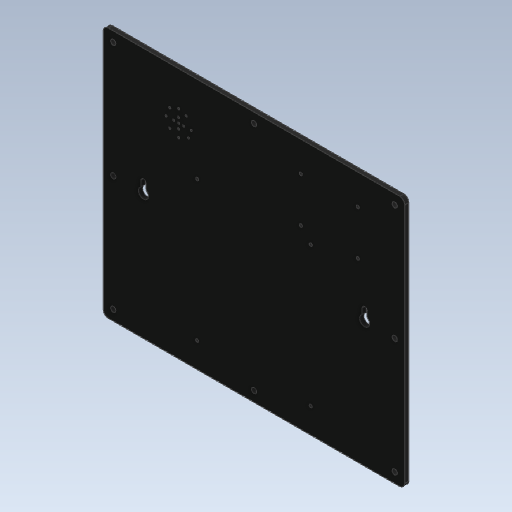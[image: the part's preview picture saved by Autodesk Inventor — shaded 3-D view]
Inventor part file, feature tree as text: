
AUTODESK INVENTOR PART (.ipt)
format: ipt  version: 2020 (Build 240168000, 168)  size: 320,000 bytes
history: native  units: mm
features: extrude x6, sketch x6, fillet x1, other x1
ambient origin geometry x8: Origin, YZ Plane, XZ Plane, XY Plane, X Axis, Y Axis, Z Axis, Center Point
bodies: Solid1 (feature_tree)
feature tree (14):
  extrude  "Extrusion1"  Depth=250.0mm
  fillet  "Fillet1"  Radius=4.0mm
  extrude  "Extrusion2"  Depth=5.0mm
  extrude  "Extrusion3"  Depth=56.5mm
  sketch  "Sketch4"  dims[d8=3.0mm d9=3.0mm]
  extrude  "Extrusion4"  Depth=3.0mm
  extrude  "Extrusion5"  Depth=139.0mm
  extrude  "Extrusion6"  Depth=10.0mm
  other  "Back-CNC-CUT"
  sketch  "Sketch1"  dims[d0=300.0mm d1=250.0mm d2=4.0mm d3=0.0mm]
  sketch  "Sketch2"  dims[d4=5.0mm d5=25.0mm]
  sketch  "Sketch3"  dims[d6=56.5mm d7=56.5mm]
  sketch  "Sketch5"  dims[d10=139.0mm d11=139.0mm]
  sketch  "Sketch6"  dims[d12=3.0mm d13=3.0mm d14=33.75mm d15=0.0mm d19=3.0mm d20=3.0mm d21=44.44mm d22=44.44mm d23=3.0mm d24=3.0mm d25=33.75mm d26=0.0mm d30=25.0mm d31=10.0mm d32=2.0mm d33=2.0mm d34=2.0mm d35=2.0mm d36=2.0mm d37=2.0mm d38=2.0mm d39=2.0mm d40=135.0deg d41=2.0mm d42=2.0mm d43=135.0deg d44=2.0mm d45=2.0mm d46=33.75mm d47=0.0mm d48=2.0mm d49=75.0mm d50=47.0mm d51=75.0mm d52=30.0mm d53=40.0mm d54=40.0mm d55=10.0mm d56=10.0mm d57=10.0mm d58=5.0mm d59=10.0mm d60=5.0mm d61=10.0mm d62=0.0mm d63=5.2mm d64=5.2mm d65=5.2mm d66=5.2mm d67=10.0mm d68=0.0mm d69=10.0mm d70=5.2mm d71=10.0mm d72=5.2mm d73=10.0mm d74=5.2mm d75=10.0mm d76=5.2mm]
